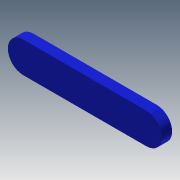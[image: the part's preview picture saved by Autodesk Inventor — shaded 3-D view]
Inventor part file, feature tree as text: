
AUTODESK INVENTOR PART (.ipt)
format: ipt  version: 2013 (Build 170138000, 138)  size: 100,864 bytes
history: native  units: mm
features: extrude x3, sketch x3
ambient origin geometry x8: Origin, YZ Plane, XZ Plane, XY Plane, X Axis, Y Axis, Z Axis, Center Point
bodies: Solid1 (feature_tree)
feature tree (6):
  extrude  "Extrusion1"  Depth=6.0mm
  extrude  "Extrusion2"  Depth=6.0mm
  extrude  "Extrusion3"  Depth=2.0mm
  sketch  "Sketch1"  dims[d0=24.0mm d1=6.0mm]
  sketch  "Sketch2"  dims[d2=6.0mm d3=6.0mm]
  sketch  "Sketch3"  dims[d4=2.0mm d5=0.0mm d6=2.0mm d7=3.0mm d8=3.0mm d9=2.0mm d10=0.0mm d11=0.01mm d12=0.01mm d13=2.0mm d14=0.0mm]
